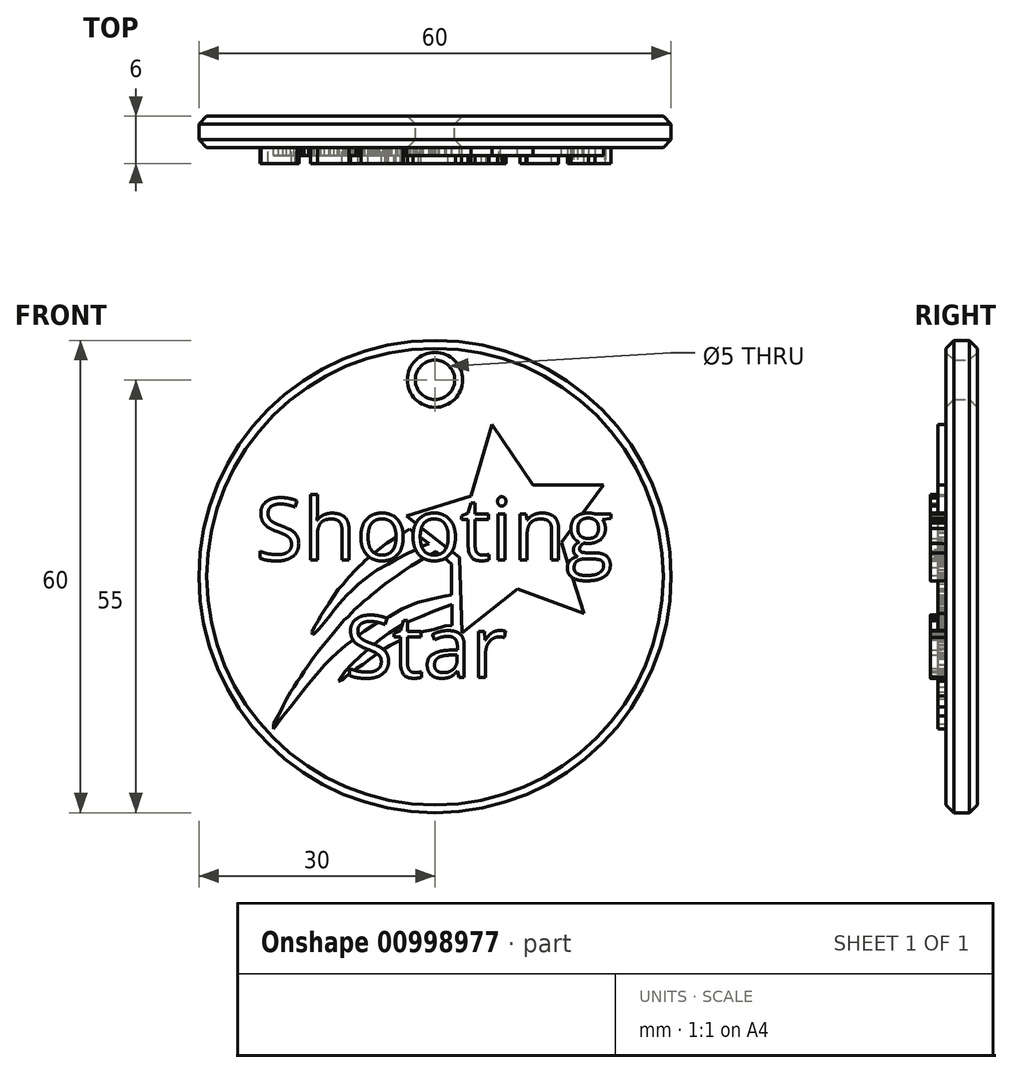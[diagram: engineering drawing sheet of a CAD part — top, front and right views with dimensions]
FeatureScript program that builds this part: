
annotation { "Feature Type Name" : "Feature", "Feature Type Description" : "" }
export const myFeature = defineFeature(function(context is Context, id is Id, definition is map)
    precondition{}
    {
        {
            var Q0;
            Q0=qCreatedBy(makeId("Front.planeOp"),FACE);
            var sketch = newSketch(context, id + "F0", { "sketchPlane" : qUnion([Q0])});
            skCircle(sketch, "E0", {"center": v(0, 0) * mm, "radius": 30 * mm});
            skLineSegment(sketch, "E1", {"start": v(-22.15, 20.23) * mm, "end": v(22.17, 20.23) * mm, "construction": true});
            skLineSegment(sketch, "E2", {"start": v(22.17, -20.13) * mm, "end": v(-22.15, -20.13) * mm, "construction": true});
            skLineSegment(sketch, "E3", {"start": v(-22.15, 20.23) * mm, "end": v(-22.15, -20.13) * mm, "construction": true});
            skLineSegment(sketch, "E4", {"start": v(22.17, 20.23) * mm, "end": v(22.17, -20.13) * mm, "construction": true});
            skLineSegment(sketch, "E5", {"start": v(0, 0) * mm, "end": v(0, 25) * mm, "construction": true});
            skCircle(sketch, "E6", {"center": v(0, 25) * mm, "radius": 2.5 * mm});
            skSolve(sketch);
        }
        {
            var Q0;
            Q0=makeQuery(id+"F0.imprint","IMPRINT",FACE,{"disambiguationData":[TD([[makeQuery(id+"F0.imprint","IMPRINT",EDGE,{"derivedFrom":sQuery(id+"F0.wireOp",EDGE,"E0")}),1.0]])]});
            extrude(context, id + "F1", {"entities" : qUnion([Q0]), "depth" : 4 * mm, "offsetDistance" : 25 * mm});
        }
        {
            var Q0;
            Q0=qCreatedBy(makeId("Front.planeOp"),FACE);
            var sketch = newSketch(context, id + "F2", { "sketchPlane" : qUnion([Q0])});
            skLineSegment(sketch, "E7", {"start": v(4.57, 10.27) * mm, "end": v(-3.64, 7.67) * mm});
            skLineSegment(sketch, "E8", {"start": v(-3.64, 7.67) * mm, "end": v(3.12, 2.43) * mm});
            skLineSegment(sketch, "E9", {"start": v(3.12, 2.43) * mm, "end": v(3.45, -7.14) * mm});
            skLineSegment(sketch, "E10", {"start": v(3.45, -7.14) * mm, "end": v(10.5, -1.54) * mm});
            skLineSegment(sketch, "E11", {"start": v(10.5, -1.54) * mm, "end": v(18.9, -4.66) * mm});
            skLineSegment(sketch, "E12", {"start": v(18.9, -4.66) * mm, "end": v(16.05, 4.3) * mm});
            skLineSegment(sketch, "E13", {"start": v(16.05, 4.3) * mm, "end": v(21.42, 11.63) * mm});
            skLineSegment(sketch, "E14", {"start": v(21.42, 11.63) * mm, "end": v(12.47, 11.63) * mm});
            skLineSegment(sketch, "E15", {"start": v(12.47, 11.63) * mm, "end": v(7.27, 19.36) * mm});
            skLineSegment(sketch, "E16", {"start": v(7.27, 19.36) * mm, "end": v(4.57, 10.27) * mm});
            skLineSegment(sketch, "E17", {"start": v(-20.5, -19.36) * mm, "end": v(-19.28, -17.7) * mm});
            skLineSegment(sketch, "E18", {"start": v(-19.28, -17.7) * mm, "end": v(-18.33, -16.56) * mm});
            skLineSegment(sketch, "E19", {"start": v(-18.33, -16.56) * mm, "end": v(-17.28, -15.13) * mm});
            skLineSegment(sketch, "E20", {"start": v(-17.28, -15.13) * mm, "end": v(-16.4, -14.04) * mm});
            skLineSegment(sketch, "E21", {"start": v(-16.4, -14.04) * mm, "end": v(-15.44, -12.88) * mm});
            skLineSegment(sketch, "E22", {"start": v(-15.44, -12.88) * mm, "end": v(-14.68, -12) * mm});
            skLineSegment(sketch, "E23", {"start": v(-14.68, -12) * mm, "end": v(-14.05, -11.24) * mm});
            skLineSegment(sketch, "E24", {"start": v(-14.05, -11.24) * mm, "end": v(-13.2, -10.41) * mm});
            skLineSegment(sketch, "E25", {"start": v(-13.2, -10.41) * mm, "end": v(-12.36, -9.6) * mm});
            skLineSegment(sketch, "E26", {"start": v(-12.36, -9.6) * mm, "end": v(-11.34, -8.74) * mm});
            skLineSegment(sketch, "E27", {"start": v(-11.34, -8.74) * mm, "end": v(-10.33, -7.93) * mm});
            skLineSegment(sketch, "E28", {"start": v(-10.33, -7.93) * mm, "end": v(-8.92, -6.92) * mm});
            skLineSegment(sketch, "E29", {"start": v(-8.92, -6.92) * mm, "end": v(-7.86, -6.23) * mm});
            skLineSegment(sketch, "E30", {"start": v(-7.86, -6.23) * mm, "end": v(-5.8, -5.05) * mm});
            skLineSegment(sketch, "E31", {"start": v(-5.8, -5.05) * mm, "end": v(-4.17, -4.08) * mm});
            skLineSegment(sketch, "E32", {"start": v(-4.17, -4.08) * mm, "end": v(-2.2, -3.3) * mm});
            skLineSegment(sketch, "E33", {"start": v(-2.2, -3.3) * mm, "end": v(-0.6, -2.87) * mm});
            skLineSegment(sketch, "E34", {"start": v(-0.6, -2.87) * mm, "end": v(0.43, -2.63) * mm});
            skLineSegment(sketch, "E35", {"start": v(0.43, -2.63) * mm, "end": v(1.33, -2.47) * mm});
            skLineSegment(sketch, "E36", {"start": v(1.33, -2.47) * mm, "end": v(2.11, -2.35) * mm});
            skLineSegment(sketch, "E37", {"start": v(2.11, -2.35) * mm, "end": v(2.11, 1.64) * mm});
            skLineSegment(sketch, "E38", {"start": v(2.11, 1.64) * mm, "end": v(0.1, 3.2) * mm});
            skLineSegment(sketch, "E39", {"start": v(0.1, 3.2) * mm, "end": v(-0.47, 2.9) * mm});
            skLineSegment(sketch, "E40", {"start": v(-0.47, 2.9) * mm, "end": v(-1.12, 2.51) * mm});
            skLineSegment(sketch, "E41", {"start": v(-1.12, 2.51) * mm, "end": v(-1.79, 2.14) * mm});
            skLineSegment(sketch, "E42", {"start": v(-1.79, 2.14) * mm, "end": v(-2.32, 1.8) * mm});
            skLineSegment(sketch, "E43", {"start": v(-2.32, 1.8) * mm, "end": v(-3.02, 1.35) * mm});
            skLineSegment(sketch, "E44", {"start": v(-3.02, 1.35) * mm, "end": v(-3.78, 0.85) * mm});
            skLineSegment(sketch, "E45", {"start": v(-3.78, 0.85) * mm, "end": v(-4.23, 0.54) * mm});
            skLineSegment(sketch, "E46", {"start": v(-4.23, 0.54) * mm, "end": v(-4.77, 0.17) * mm});
            skLineSegment(sketch, "E47", {"start": v(-4.77, 0.17) * mm, "end": v(-5.7, -0.51) * mm});
            skLineSegment(sketch, "E48", {"start": v(-5.7, -0.51) * mm, "end": v(-6.34, -0.94) * mm});
            skLineSegment(sketch, "E49", {"start": v(-6.34, -0.94) * mm, "end": v(-7.03, -1.52) * mm});
            skLineSegment(sketch, "E50", {"start": v(-7.03, -1.52) * mm, "end": v(-7.51, -1.87) * mm});
            skLineSegment(sketch, "E51", {"start": v(-7.51, -1.87) * mm, "end": v(-8.05, -2.33) * mm});
            skLineSegment(sketch, "E52", {"start": v(-8.05, -2.33) * mm, "end": v(-8.44, -2.68) * mm});
            skLineSegment(sketch, "E53", {"start": v(-8.44, -2.68) * mm, "end": v(-9.02, -3.07) * mm});
            skLineSegment(sketch, "E54", {"start": v(-9.02, -3.07) * mm, "end": v(-9.5, -3.53) * mm});
            skLineSegment(sketch, "E55", {"start": v(-9.5, -3.53) * mm, "end": v(-9.91, -3.9) * mm});
            skLineSegment(sketch, "E56", {"start": v(-9.91, -3.9) * mm, "end": v(-10.2, -4.15) * mm});
            skLineSegment(sketch, "E57", {"start": v(-10.2, -4.15) * mm, "end": v(-10.57, -4.53) * mm});
            skLineSegment(sketch, "E58", {"start": v(-10.57, -4.53) * mm, "end": v(-11.07, -5.1) * mm});
            skLineSegment(sketch, "E59", {"start": v(-11.07, -5.1) * mm, "end": v(-11.57, -5.5) * mm});
            skLineSegment(sketch, "E60", {"start": v(-11.57, -5.5) * mm, "end": v(-13.16, -7.44) * mm});
            skLineSegment(sketch, "E61", {"start": v(-13.16, -7.44) * mm, "end": v(-14.5, -9.07) * mm});
            skLineSegment(sketch, "E62", {"start": v(-14.5, -9.07) * mm, "end": v(-14.95, -9.67) * mm});
            skLineSegment(sketch, "E63", {"start": v(-14.95, -9.67) * mm, "end": v(-15.36, -10.19) * mm});
            skLineSegment(sketch, "E64", {"start": v(-15.36, -10.19) * mm, "end": v(-15.67, -10.64) * mm});
            skLineSegment(sketch, "E65", {"start": v(-15.67, -10.64) * mm, "end": v(-16.07, -11.2) * mm});
            skLineSegment(sketch, "E66", {"start": v(-16.07, -11.2) * mm, "end": v(-16.65, -12.06) * mm});
            skLineSegment(sketch, "E67", {"start": v(-16.65, -12.06) * mm, "end": v(-17.02, -12.65) * mm});
            skLineSegment(sketch, "E68", {"start": v(-17.02, -12.65) * mm, "end": v(-17.5, -13.36) * mm});
            skLineSegment(sketch, "E69", {"start": v(-17.5, -13.36) * mm, "end": v(-17.92, -14.02) * mm});
            skLineSegment(sketch, "E70", {"start": v(-17.92, -14.02) * mm, "end": v(-18.34, -14.68) * mm});
            skLineSegment(sketch, "E71", {"start": v(-18.34, -14.68) * mm, "end": v(-18.86, -15.55) * mm});
            skLineSegment(sketch, "E72", {"start": v(-18.86, -15.55) * mm, "end": v(-19.3, -16.4) * mm});
            skLineSegment(sketch, "E73", {"start": v(-19.3, -16.4) * mm, "end": v(-19.9, -17.62) * mm});
            skLineSegment(sketch, "E74", {"start": v(-19.9, -17.62) * mm, "end": v(-20.48, -18.7) * mm});
            skLineSegment(sketch, "E75", {"start": v(-20.48, -18.7) * mm, "end": v(-20.5, -19.36) * mm});
            skLineSegment(sketch, "E76", {"start": v(-12.23, -13.23) * mm, "end": v(-11.4, -12.06) * mm});
            skLineSegment(sketch, "E77", {"start": v(-11.4, -12.06) * mm, "end": v(-10.59, -11.17) * mm});
            skLineSegment(sketch, "E78", {"start": v(-10.59, -11.17) * mm, "end": v(-9.4, -10.04) * mm});
            skLineSegment(sketch, "E79", {"start": v(-9.4, -10.04) * mm, "end": v(-8.34, -9.13) * mm});
            skLineSegment(sketch, "E80", {"start": v(-8.34, -9.13) * mm, "end": v(-6.98, -8.01) * mm});
            skLineSegment(sketch, "E81", {"start": v(-6.98, -8.01) * mm, "end": v(-5.83, -7.18) * mm});
            skLineSegment(sketch, "E82", {"start": v(-5.83, -7.18) * mm, "end": v(-4.72, -6.45) * mm});
            skLineSegment(sketch, "E83", {"start": v(-4.72, -6.45) * mm, "end": v(-3.3, -5.72) * mm});
            skLineSegment(sketch, "E84", {"start": v(-3.3, -5.72) * mm, "end": v(-1.72, -5.03) * mm});
            skLineSegment(sketch, "E85", {"start": v(-1.72, -5.03) * mm, "end": v(-0.24, -4.44) * mm});
            skLineSegment(sketch, "E86", {"start": v(-0.24, -4.44) * mm, "end": v(1.25, -3.87) * mm});
            skLineSegment(sketch, "E87", {"start": v(1.25, -3.87) * mm, "end": v(2.2, -3.55) * mm});
            skLineSegment(sketch, "E88", {"start": v(2.2, -3.55) * mm, "end": v(2.2, -6.19) * mm});
            skLineSegment(sketch, "E89", {"start": v(2.2, -6.19) * mm, "end": v(1.27, -6.27) * mm});
            skLineSegment(sketch, "E90", {"start": v(1.27, -6.27) * mm, "end": v(-0.13, -6.7) * mm});
            skLineSegment(sketch, "E91", {"start": v(-0.13, -6.7) * mm, "end": v(-1.81, -7.07) * mm});
            skLineSegment(sketch, "E92", {"start": v(-1.81, -7.07) * mm, "end": v(-2.93, -7.51) * mm});
            skLineSegment(sketch, "E93", {"start": v(-2.93, -7.51) * mm, "end": v(-3.97, -7.85) * mm});
            skLineSegment(sketch, "E94", {"start": v(-3.97, -7.85) * mm, "end": v(-4.84, -8.31) * mm});
            skLineSegment(sketch, "E95", {"start": v(-4.84, -8.31) * mm, "end": v(-5.7, -8.75) * mm});
            skLineSegment(sketch, "E96", {"start": v(-5.7, -8.75) * mm, "end": v(-6.6, -9.31) * mm});
            skLineSegment(sketch, "E97", {"start": v(-6.6, -9.31) * mm, "end": v(-7.35, -9.84) * mm});
            skLineSegment(sketch, "E98", {"start": v(-7.35, -9.84) * mm, "end": v(-8.23, -10.43) * mm});
            skLineSegment(sketch, "E99", {"start": v(-8.23, -10.43) * mm, "end": v(-9.17, -11.13) * mm});
            skLineSegment(sketch, "E100", {"start": v(-9.17, -11.13) * mm, "end": v(-9.94, -11.67) * mm});
            skLineSegment(sketch, "E101", {"start": v(-9.94, -11.67) * mm, "end": v(-10.45, -12.04) * mm});
            skLineSegment(sketch, "E102", {"start": v(-10.45, -12.04) * mm, "end": v(-11, -12.42) * mm});
            skLineSegment(sketch, "E103", {"start": v(-11, -12.42) * mm, "end": v(-11.34, -12.76) * mm});
            skLineSegment(sketch, "E104", {"start": v(-11.34, -12.76) * mm, "end": v(-11.7, -13.1) * mm});
            skLineSegment(sketch, "E105", {"start": v(-11.7, -13.1) * mm, "end": v(-12.1, -13.26) * mm});
            skLineSegment(sketch, "E106", {"start": v(-12.1, -13.26) * mm, "end": v(-12.23, -13.23) * mm});
            skLineSegment(sketch, "E107", {"start": v(-15.55, -7.37) * mm, "end": v(-15.64, -7.03) * mm});
            skLineSegment(sketch, "E108", {"start": v(-15.64, -7.03) * mm, "end": v(-15.27, -6.34) * mm});
            skLineSegment(sketch, "E109", {"start": v(-15.27, -6.34) * mm, "end": v(-14.8, -5.59) * mm});
            skLineSegment(sketch, "E110", {"start": v(-14.8, -5.59) * mm, "end": v(-14.51, -4.98) * mm});
            skLineSegment(sketch, "E111", {"start": v(-14.51, -4.98) * mm, "end": v(-14.03, -4.21) * mm});
            skLineSegment(sketch, "E112", {"start": v(-14.03, -4.21) * mm, "end": v(-13.44, -3.4) * mm});
            skLineSegment(sketch, "E113", {"start": v(-13.44, -3.4) * mm, "end": v(-12.86, -2.5) * mm});
            skLineSegment(sketch, "E114", {"start": v(-12.86, -2.5) * mm, "end": v(-12.29, -1.65) * mm});
            skLineSegment(sketch, "E115", {"start": v(-12.29, -1.65) * mm, "end": v(-11.71, -0.98) * mm});
            skLineSegment(sketch, "E116", {"start": v(-11.71, -0.98) * mm, "end": v(-11.26, -0.44) * mm});
            skLineSegment(sketch, "E117", {"start": v(-11.26, -0.44) * mm, "end": v(-10.92, -0.07) * mm});
            skLineSegment(sketch, "E118", {"start": v(-10.92, -0.07) * mm, "end": v(-10.06, 0.93) * mm});
            skLineSegment(sketch, "E119", {"start": v(-10.06, 0.93) * mm, "end": v(-9.64, 1.26) * mm});
            skLineSegment(sketch, "E120", {"start": v(-9.64, 1.26) * mm, "end": v(-9.3, 1.63) * mm});
            skLineSegment(sketch, "E121", {"start": v(-9.3, 1.63) * mm, "end": v(-8.87, 2.06) * mm});
            skLineSegment(sketch, "E122", {"start": v(-8.87, 2.06) * mm, "end": v(-8.4, 2.44) * mm});
            skLineSegment(sketch, "E123", {"start": v(-8.4, 2.44) * mm, "end": v(-7.94, 2.84) * mm});
            skLineSegment(sketch, "E124", {"start": v(-7.94, 2.84) * mm, "end": v(-7.32, 3.3) * mm});
            skLineSegment(sketch, "E125", {"start": v(-7.32, 3.3) * mm, "end": v(-6.6, 3.86) * mm});
            skLineSegment(sketch, "E126", {"start": v(-6.6, 3.86) * mm, "end": v(-6.1, 4.24) * mm});
            skLineSegment(sketch, "E127", {"start": v(-6.1, 4.24) * mm, "end": v(-5.43, 4.64) * mm});
            skLineSegment(sketch, "E128", {"start": v(-5.43, 4.64) * mm, "end": v(-4.79, 5.06) * mm});
            skLineSegment(sketch, "E129", {"start": v(-4.79, 5.06) * mm, "end": v(-4.31, 5.36) * mm});
            skLineSegment(sketch, "E130", {"start": v(-4.31, 5.36) * mm, "end": v(-3.82, 5.67) * mm});
            skLineSegment(sketch, "E131", {"start": v(-3.82, 5.67) * mm, "end": v(-3.26, 6.05) * mm});
            skLineSegment(sketch, "E132", {"start": v(-3.26, 6.05) * mm, "end": v(-1.97, 5.09) * mm});
            skLineSegment(sketch, "E133", {"start": v(-1.97, 5.09) * mm, "end": v(-0.74, 4.22) * mm});
            skLineSegment(sketch, "E134", {"start": v(-0.74, 4.22) * mm, "end": v(-1.5, 3.89) * mm});
            skLineSegment(sketch, "E135", {"start": v(-1.5, 3.89) * mm, "end": v(-2, 3.62) * mm});
            skLineSegment(sketch, "E136", {"start": v(-2, 3.62) * mm, "end": v(-3.36, 3) * mm});
            skLineSegment(sketch, "E137", {"start": v(-3.36, 3) * mm, "end": v(-4.97, 2.2) * mm});
            skLineSegment(sketch, "E138", {"start": v(-4.97, 2.2) * mm, "end": v(-5.92, 1.64) * mm});
            skLineSegment(sketch, "E139", {"start": v(-5.92, 1.64) * mm, "end": v(-7.34, 0.82) * mm});
            skLineSegment(sketch, "E140", {"start": v(-7.34, 0.82) * mm, "end": v(-8.05, 0.36) * mm});
            skLineSegment(sketch, "E141", {"start": v(-8.05, 0.36) * mm, "end": v(-8.9, -0.27) * mm});
            skLineSegment(sketch, "E142", {"start": v(-8.9, -0.27) * mm, "end": v(-9.69, -0.93) * mm});
            skLineSegment(sketch, "E143", {"start": v(-9.69, -0.93) * mm, "end": v(-10.56, -1.74) * mm});
            skLineSegment(sketch, "E144", {"start": v(-10.56, -1.74) * mm, "end": v(-11.2, -2.37) * mm});
            skLineSegment(sketch, "E145", {"start": v(-11.2, -2.37) * mm, "end": v(-11.55, -2.75) * mm});
            skLineSegment(sketch, "E146", {"start": v(-11.55, -2.75) * mm, "end": v(-12.15, -3.41) * mm});
            skLineSegment(sketch, "E147", {"start": v(-12.15, -3.41) * mm, "end": v(-12.8, -4.24) * mm});
            skLineSegment(sketch, "E148", {"start": v(-12.8, -4.24) * mm, "end": v(-13.28, -4.84) * mm});
            skLineSegment(sketch, "E149", {"start": v(-13.28, -4.84) * mm, "end": v(-14.1, -5.89) * mm});
            skLineSegment(sketch, "E150", {"start": v(-14.1, -5.89) * mm, "end": v(-14.72, -6.68) * mm});
            skLineSegment(sketch, "E151", {"start": v(-14.72, -6.68) * mm, "end": v(-14.98, -6.9) * mm});
            skLineSegment(sketch, "E152", {"start": v(-14.98, -6.9) * mm, "end": v(-15.3, -7.2) * mm});
            skLineSegment(sketch, "E153", {"start": v(-15.3, -7.2) * mm, "end": v(-15.55, -7.37) * mm});
            skSolve(sketch);
        }
        {
            var Q0;
            Q0 = qSketchRegion(id + "F2", true);
            extrude(context, id + "F3", {"entities" : qUnion([Q0]), "operationType" : NewBodyOperationType.ADD, "depth" : 5 * mm, "offsetDistance" : 25 * mm, "hasSecondDirection" : true, "secondDirectionOppositeDirection" : false, "secondDirectionDepth" : 2.7 * mm});
        }
        {
            var Q0;
            Q0=qCreatedBy(makeId("Front.planeOp"),FACE);
            var sketch = newSketch(context, id + "F4", { "sketchPlane" : qUnion([Q0])});
            skText(sketch, "E154", { "text": "Shooting\n    Star", "fontName": "OpenSans-Regular.ttf"});
            const initialGuessF4  = {"E154": [-0.0228, 0.0021, 1, 0, 0.0079]};
            skSetInitialGuess(sketch, initialGuessF4);
            skSolve(sketch);
        }
        {
            var Q0;
            Q0 = qSketchRegion(id + "F4", true);
            extrude(context, id + "F5", {"entities" : qUnion([Q0]), "operationType" : NewBodyOperationType.ADD, "depth" : 6 * mm, "offsetDistance" : 25 * mm});
        }
        {
            var Q0;
            Q0=makeQuery(id+"F1.opExtrude","CAP_EDGE",EDGE,{"disambiguationData":[OSD([sQuery(id+"F0.wireOp",EDGE,"E0")])],"isStart":false});
            var Q1;
            Q1=makeQuery(id+"F1.opExtrude","CAP_EDGE",EDGE,{"disambiguationData":[OSD([sQuery(id+"F0.wireOp",EDGE,"E0")])],"isStart":true});
            var Q2;
            Q2=makeQuery(id+"F1.opExtrude","CAP_EDGE",EDGE,{"disambiguationData":[OSD([sQuery(id+"F0.wireOp",EDGE,"E6")])],"isStart":false});
            var Q3;
            Q3=makeQuery(id+"F1.opExtrude","CAP_EDGE",EDGE,{"disambiguationData":[OSD([sQuery(id+"F0.wireOp",EDGE,"E6")])],"isStart":true});
            chamfer(context, id + "F6", {"entities" : qUnion([Q0, Q1, Q2, Q3]), "width" : 1 * mm, "tangentPropagation" : true});
        }
    });
